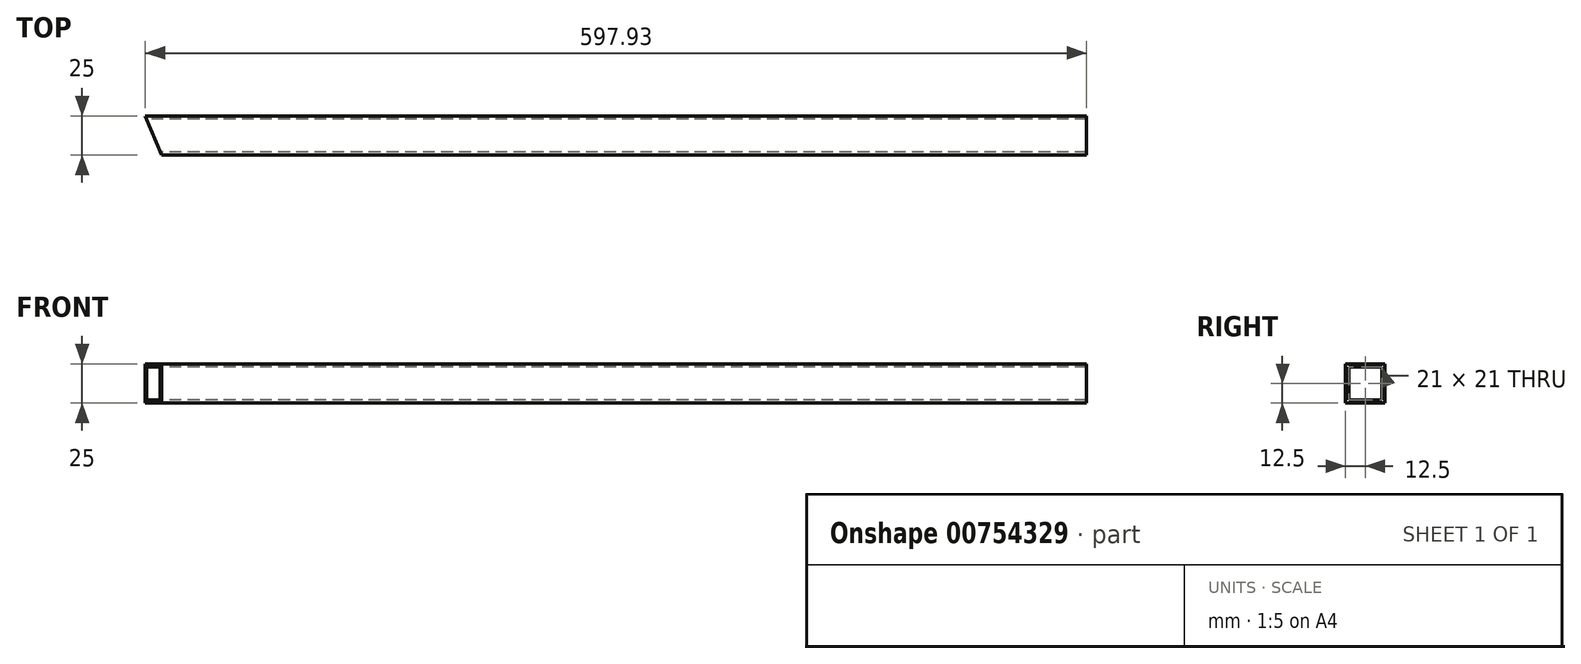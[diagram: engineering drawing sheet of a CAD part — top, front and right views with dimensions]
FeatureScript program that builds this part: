
annotation { "Feature Type Name" : "Feature", "Feature Type Description" : "" }
export const myFeature = defineFeature(function(context is Context, id is Id, definition is map)
    precondition{}
    {
        {
            var Q0;
            Q0=qCreatedBy(makeId("Right.planeOp"),FACE);
            var sketch = newSketch(context, id + "F0", { "sketchPlane" : qUnion([Q0])});
            skLineSegment(sketch, "E0.bottom", {"start": v(12.5, 12.5) * mm, "end": v(-12.5, 12.5) * mm});
            skLineSegment(sketch, "E0.top", {"start": v(12.5, -12.5) * mm, "end": v(-12.5, -12.5) * mm});
            skLineSegment(sketch, "E0.left", {"start": v(12.5, 12.5) * mm, "end": v(12.5, -12.5) * mm});
            skLineSegment(sketch, "E0.right", {"start": v(-12.5, 12.5) * mm, "end": v(-12.5, -12.5) * mm});
            skPoint(sketch, "E0.middle", {"position": v(0, 0) * mm});
            skLineSegment(sketch, "E1.bottom", {"start": v(10.5, 10.5) * mm, "end": v(-10.5, 10.5) * mm});
            skLineSegment(sketch, "E1.top", {"start": v(10.5, -10.5) * mm, "end": v(-10.5, -10.5) * mm});
            skLineSegment(sketch, "E1.left", {"start": v(10.5, 10.5) * mm, "end": v(10.5, -10.5) * mm});
            skLineSegment(sketch, "E1.right", {"start": v(-10.5, 10.5) * mm, "end": v(-10.5, -10.5) * mm});
            skLineSegment(sketch, "E2", {"start": v(-10.5, 10.5) * mm, "end": v(-10.5, 12.5) * mm, "construction": true});
            skLineSegment(sketch, "E3", {"start": v(-10.5, 10.5) * mm, "end": v(-12.5, 10.5) * mm, "construction": true});
            skSolve(sketch);
        }
        {
            var Q0;
            Q0 = qSketchRegion(id + "F0", true);
            extrude(context, id + "F1", {"entities" : qUnion([Q0]), "depth" : 600 * mm, "offsetDistance" : 25 * mm});
        }
        {
            var Q0;
            Q0=makeQuery(id+"F1.opExtrude","CAP_EDGE",EDGE,{"disambiguationData":[OSD([sQuery(id+"F0.wireOp",EDGE,"E0.right")])],"isStart":true});
            chamfer(context, id + "F2", {"entities" : qUnion([Q0]), "chamferType" : ChamferType.OFFSET_ANGLE, "width" : 30 * mm, "oppositeDirection" : true, "angle" : 22.5 * degree, "tangentPropagation" : true});
        }
    });
